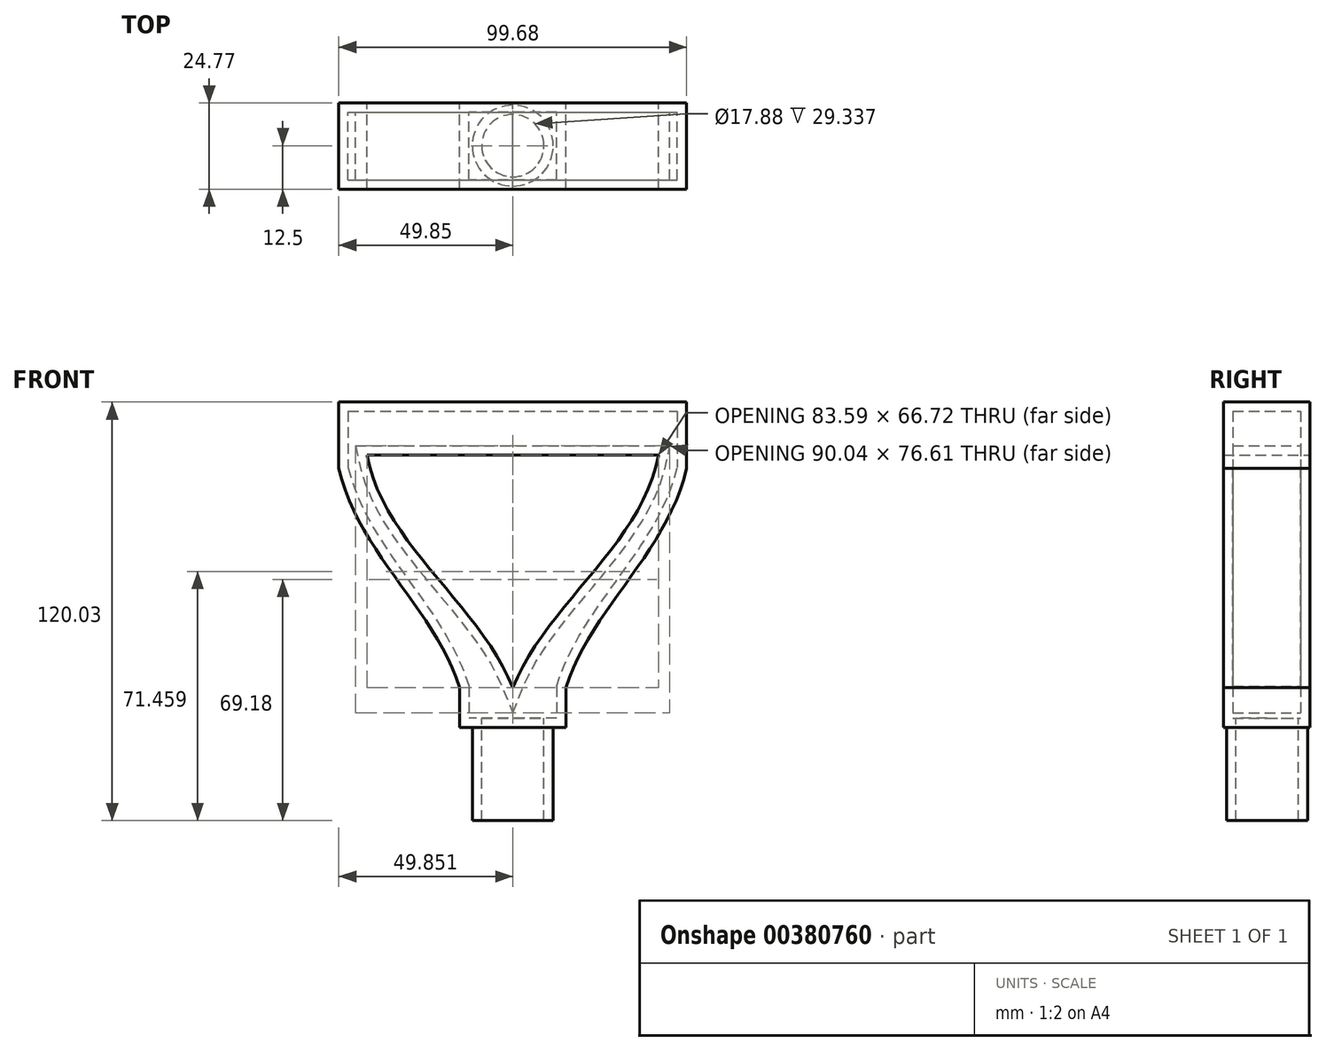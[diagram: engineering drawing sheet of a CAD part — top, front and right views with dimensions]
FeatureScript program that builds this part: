
annotation { "Feature Type Name" : "Feature", "Feature Type Description" : "" }
export const myFeature = defineFeature(function(context is Context, id is Id, definition is map)
    precondition{}
    {
        {
            var Q0;
            Q0=qCreatedBy(makeId("Front.planeOp"),FACE);
            var sketch = newSketch(context, id + "F0", { "sketchPlane" : qUnion([Q0])});
            skLineSegment(sketch, "E0", {"start": v(-33.23, 54.62) * mm, "end": v(0, 54.62) * mm});
            skLineSegment(sketch, "E1", {"start": v(33.22, 54.62) * mm, "end": v(0, 54.62) * mm});
            skLineSegment(sketch, "E2", {"start": v(-33.23, 54.62) * mm, "end": v(-33.23, 41.92) * mm});
            skLineSegment(sketch, "E3", {"start": v(33.22, 54.62) * mm, "end": v(33.22, 41.92) * mm});
            skFitSpline(sketch, "E4", {"points": [v(-33.23, 41.92) * mm, v(-10.16, 0) * mm], "startDerivative": vector(11.5, -49.08) * mm, "endDerivative": vector(14, -45.25) * mm});
            skFitSpline(sketch, "E5", {"points": [v(10.16, 0) * mm, v(33.22, 41.92) * mm], "startDerivative": vector(14.02, 45.25) * mm, "endDerivative": vector(11.5, 49.08) * mm});
            skLineSegment(sketch, "E6", {"start": v(-27.86, 44.48) * mm, "end": v(0, 44.48) * mm});
            skLineSegment(sketch, "E7", {"start": v(0, 44.48) * mm, "end": v(27.86, 44.48) * mm});
            skFitSpline(sketch, "E8", {"points": [v(-27.86, 44.48) * mm, v(0, 0) * mm], "startDerivative": vector(9.97, -52.15) * mm, "endDerivative": vector(19.17, -48.31) * mm});
            skFitSpline(sketch, "E9", {"points": [v(0, 0) * mm, v(27.86, 44.48) * mm], "startDerivative": vector(19.2, 48.31) * mm, "endDerivative": vector(9.98, 52.15) * mm});
            skLineSegment(sketch, "E10", {"start": v(-10.16, 0) * mm, "end": v(-10.16, -7.62) * mm});
            skLineSegment(sketch, "E11", {"start": v(10.16, 0) * mm, "end": v(10.16, -7.62) * mm});
            skLineSegment(sketch, "E12", {"start": v(10.16, -7.62) * mm, "end": v(-10.16, -7.62) * mm});
            skSolve(sketch);
        }
        {
            var Q0;
            Q0 = qSketchRegion(id + "F0", true);
            extrude(context, id + "F1", {"entities" : qUnion([Q0]), "depth" : 16.5 * mm});
        }
        {
            var Q0;
            Q0=qCreatedBy(makeId("Top.planeOp"),FACE);
            var sketch = newSketch(context, id + "F2", { "sketchPlane" : qUnion([Q0])});
            skCircle(sketch, "E13", {"center": v(0, -8.18) * mm, "radius": 7.74 * mm});
            skSolve(sketch);
        }
        {
            var Q0;
            Q0 = qSketchRegion(id + "F2", true);
            extrude(context, id + "F3", {"entities" : qUnion([Q0]), "operationType" : NewBodyOperationType.ADD, "oppositeDirection" : true, "depth" : 25.4 * mm});
        }
        {
            var Q0;
            Q0=makeQuery(id+"F3.opExtrude","CAP_FACE",FACE,{"disambiguationData":[OSD([sQuery(id+"F2.wireOp",EDGE,"E13")])],"isStart":false});
            shell(context, id + "F4", {"entities" : qUnion([Q0]), "thickness" : 1.78 * mm});
        }
        {
            var Q0;
            Q0=makeQuery(id+"F1.opExtrude","SWEPT_BODY",BODY,{"disambiguationData":[OSD([sQuery(id+"F0.wireOp",EDGE,"E0"),sQuery(id+"F0.wireOp",EDGE,"E1"),sQuery(id+"F0.wireOp",EDGE,"E2"),sQuery(id+"F0.wireOp",EDGE,"E3"),sQuery(id+"F0.wireOp",EDGE,"E4"),sQuery(id+"F0.wireOp",EDGE,"E5"),sQuery(id+"F0.wireOp",EDGE,"E6"),sQuery(id+"F0.wireOp",EDGE,"E7"),sQuery(id+"F0.wireOp",EDGE,"E8"),sQuery(id+"F0.wireOp",EDGE,"E9"),sQuery(id+"F0.wireOp",EDGE,"E10"),sQuery(id+"F0.wireOp",EDGE,"E11"),sQuery(id+"F0.wireOp",EDGE,"E12")])]});
            var Q1;
            Q1=qCreatedBy(makeId("Origin.pointOp"),VERTEX);
            transform(context, id + "F5", {"entities" : qUnion([Q0]), "transformType" : TransformType.SCALE_UNIFORMLY, "scale" : 1.5, "scalePoint" : qUnion([Q1]), "makeCopy" : false});
        }
    });
